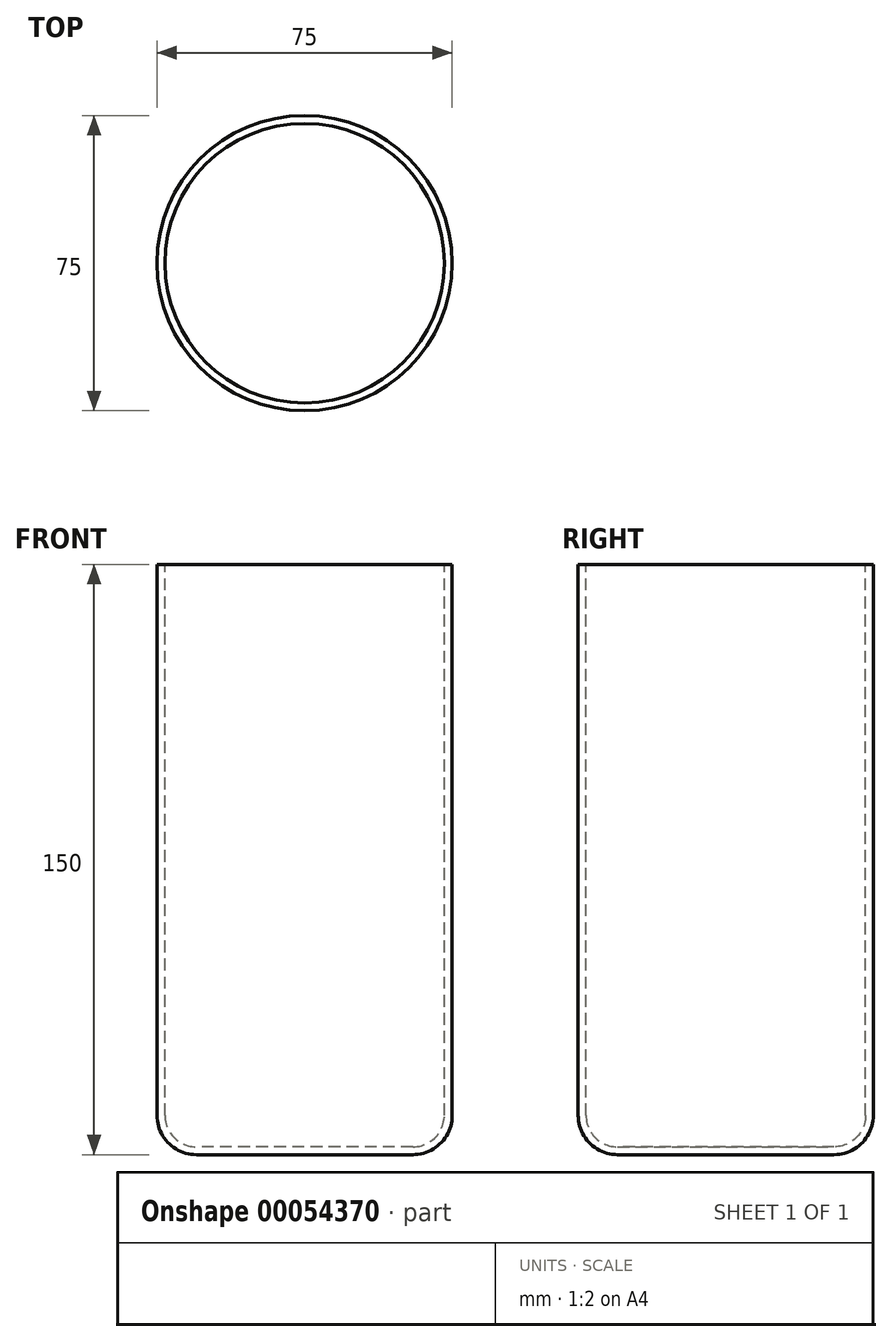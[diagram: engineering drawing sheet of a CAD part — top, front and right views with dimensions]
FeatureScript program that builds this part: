
annotation { "Feature Type Name" : "Feature", "Feature Type Description" : "" }
export const myFeature = defineFeature(function(context is Context, id is Id, definition is map)
    precondition{}
    {
        {
            var Q0;
            Q0=qCreatedBy(makeId("Front.planeOp"),FACE);
            var sketch = newSketch(context, id + "F0", { "sketchPlane" : qUnion([Q0])});
            skLineSegment(sketch, "E0.rect.bottom", {"start": v(-37.5, 75) * mm, "end": v(0, 75) * mm});
            skLineSegment(sketch, "E0.rect.top", {"start": v(-27.5, -75) * mm, "end": v(0, -75) * mm});
            skLineSegment(sketch, "E0.rect.left", {"start": v(-37.5, 75) * mm, "end": v(-37.5, -65) * mm});
            skPoint(sketch, "E0.rect.middle", {"position": v(0, 0) * mm});
            skLineSegment(sketch, "E1", {"start": v(0, 75) * mm, "end": v(0, -75) * mm, "construction": true});
            skPoint(sketch, "E0.rect.right.start.orphan", {"position": v(37.5, 75) * mm});
            skPoint(sketch, "E2.orphan", {"position": v(37.5, -75) * mm});
            skPoint(sketch, "E3.visualSharp", {"position": v(-37.5, -75) * mm});
            skArc(sketch, "E3.filletArc", {"start": v(-37.5, -65) * mm, "mid": v(-34.57, -72.07) * mm, "end": v(-27.5, -75) * mm});
            skLineSegment(sketch, "E4", {"start": v(0, 75) * mm, "end": v(0, -75) * mm});
            skSolve(sketch);
        }
        {
            var Q0;
            Q0 = qSketchRegion(id + "F0", true);
            var Q1;
            Q1=sQuery(id+"F0.wireOp",EDGE,"E1");
            revolve(context, id + "F1", {"entities" : qUnion([Q0]), "axis" : qUnion([Q1]), "revolveType" : RevolveType.FULL});
        }
        {
            var Q0;
            Q0=makeQuery(id+"F1.opRevolve","SWEPT_FACE",FACE,{"disambiguationData":[OSD([sQuery(id+"F0.wireOp",EDGE,"E0.rect.bottom")])]});
            shell(context, id + "F2", {"entities" : qUnion([Q0]), "thickness" : 2 * mm});
        }
    });
